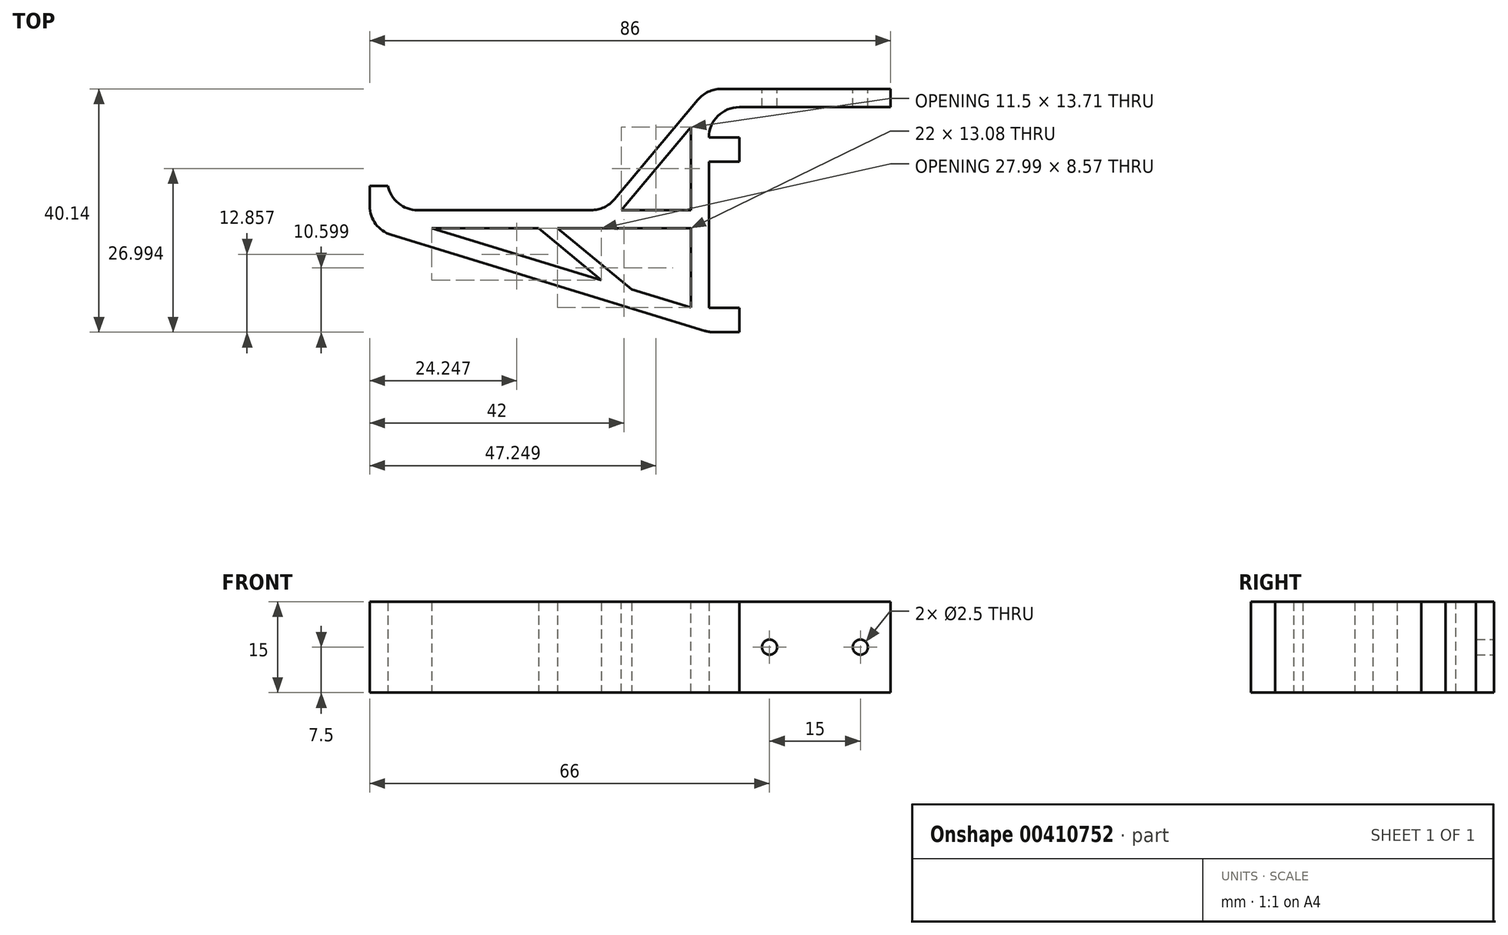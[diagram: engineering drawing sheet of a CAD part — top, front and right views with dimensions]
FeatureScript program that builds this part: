
annotation { "Feature Type Name" : "Feature", "Feature Type Description" : "" }
export const myFeature = defineFeature(function(context is Context, id is Id, definition is map)
    precondition{}
    {
        {
            var Q0;
            Q0=qCreatedBy(makeId("Top.planeOp"),FACE);
            var sketch = newSketch(context, id + "F0", { "sketchPlane" : qUnion([Q0])});
            skLineSegment(sketch, "E0", {"start": v(0, 23) * mm, "end": v(-33, 23) * mm});
            skLineSegment(sketch, "E1", {"start": v(-33, 23) * mm, "end": v(-33, 3) * mm});
            skLineSegment(sketch, "E2", {"start": v(-33, 3) * mm, "end": v(-83, 3) * mm});
            skLineSegment(sketch, "E3", {"start": v(-83, 3) * mm, "end": v(-83, 7) * mm});
            skLineSegment(sketch, "E4", {"start": v(-83, 7) * mm, "end": v(-86, 7) * mm});
            skLineSegment(sketch, "E5", {"start": v(-86, 7) * mm, "end": v(-86, 0) * mm});
            skLineSegment(sketch, "E6", {"start": v(-75.75, 0) * mm, "end": v(-58.14, 0) * mm});
            skLineSegment(sketch, "E7", {"start": v(-30, 0) * mm, "end": v(-30, 20) * mm});
            skLineSegment(sketch, "E8", {"start": v(-30, 20) * mm, "end": v(0, 20) * mm});
            skLineSegment(sketch, "E9", {"start": v(0, 20) * mm, "end": v(0, 23) * mm});
            skLineSegment(sketch, "E10", {"start": v(-86, 0) * mm, "end": v(-30, -17.14) * mm});
            skLineSegment(sketch, "E11", {"start": v(-30, -17.14) * mm, "end": v(-30, -14) * mm});
            skLineSegment(sketch, "E12", {"start": v(-33, -13.08) * mm, "end": v(-42.76, -10.1) * mm});
            skLineSegment(sketch, "E13", {"start": v(-47.76, -8.57) * mm, "end": v(-58.14, 0) * mm});
            skLineSegment(sketch, "E14", {"start": v(-42.76, -10.1) * mm, "end": v(-55, 0) * mm});
            skLineSegment(sketch, "E15.trimOffspring", {"start": v(-55, 0) * mm, "end": v(-33, 0) * mm});
            skLineSegment(sketch, "E16.trimOffspring", {"start": v(-47.76, -8.57) * mm, "end": v(-75.75, 0) * mm});
            skLineSegment(sketch, "E17", {"start": v(-30, -14) * mm, "end": v(-30, 0) * mm});
            skLineSegment(sketch, "E18", {"start": v(-33, -13.08) * mm, "end": v(-33, 0) * mm});
            skSolve(sketch);
        }
        {
            var Q0;
            Q0=makeQuery(id+"F0.imprint","IMPRINT",FACE,{"disambiguationData":[TD([[makeQuery(id+"F0.imprint","IMPRINT",EDGE,{"derivedFrom":sQuery(id+"F0.wireOp",EDGE,"E0")}),1.0]])]});
            extrude(context, id + "F1", {"entities" : qUnion([Q0]), "depth" : 15 * mm});
        }
        {
            var Q0;
            Q0=makeQuery(id+"F1.opExtrude","SWEPT_FACE",FACE,{"disambiguationData":[OSD([sQuery(id+"F0.wireOp",EDGE,"E0")])]});
            var sketch = newSketch(context, id + "F2", { "sketchPlane" : qUnion([Q0])});
            skCircle(sketch, "E19", {"center": v(5, 7.5) * mm, "radius": 1.25 * mm});
            skCircle(sketch, "E20", {"center": v(20, 7.5) * mm, "radius": 1.25 * mm});
            skSolve(sketch);
        }
        {
            var Q0;
            Q0=makeQuery(id+"F2.imprint","IMPRINT",FACE,{"disambiguationData":[TD([[makeQuery(id+"F2.imprint","IMPRINT",EDGE,{"derivedFrom":sQuery(id+"F2.wireOp",EDGE,"E19")}),1.0]])]});
            var Q1;
            Q1=makeQuery(id+"F2.imprint","IMPRINT",FACE,{"disambiguationData":[TD([[makeQuery(id+"F2.imprint","IMPRINT",EDGE,{"derivedFrom":sQuery(id+"F2.wireOp",EDGE,"E20")}),1.0]])]});
            extrude(context, id + "F3", {"entities" : qUnion([Q0, Q1]), "operationType" : NewBodyOperationType.REMOVE, "endBound" : BoundingType.THROUGH_ALL, "oppositeDirection" : true, "depth" : 25 * mm});
        }
        {
            var Q0;
            Q0=makeQuery(id+"F1.opExtrude","SWEPT_EDGE",EDGE,{"disambiguationData":[OSD([sQuery(id+"F0.wireOp",EDGE,"E0"),sQuery(id+"F0.wireOp",EDGE,"E1")])]});
            var Q1;
            Q1=makeQuery(id+"F1.opExtrude","SWEPT_EDGE",EDGE,{"disambiguationData":[OSD([sQuery(id+"F0.wireOp",EDGE,"E7"),sQuery(id+"F0.wireOp",EDGE,"E8")])]});
            fillet(context, id + "F4", {"entities" : qUnion([Q0, Q1]), "tangentPropagation" : true, "radius" : 5 * mm, "defaultsChanged" : false, "vertexSettings" : [], "allowEdgeOverflow" : false});
        }
        {
            var Q0;
            Q0=makeQuery(id+"F1.opExtrude","SWEPT_FACE",FACE,{"disambiguationData":[OSD([sQuery(id+"F0.wireOp",EDGE,"E7"),sQuery(id+"F0.wireOp",EDGE,"E11"),sQuery(id+"F0.wireOp",EDGE,"E17")])]});
            var sketch = newSketch(context, id + "F5", { "sketchPlane" : qUnion([Q0])});
            skLineSegment(sketch, "E21.bottom", {"start": v(-17.14, 15) * mm, "end": v(-13.14, 15) * mm});
            skLineSegment(sketch, "E21.top", {"start": v(-17.14, 0) * mm, "end": v(-13.14, 0) * mm});
            skLineSegment(sketch, "E21.left", {"start": v(-17.14, 15) * mm, "end": v(-17.14, 0) * mm});
            skLineSegment(sketch, "E21.right", {"start": v(-13.14, 15) * mm, "end": v(-13.14, 0) * mm});
            skLineSegment(sketch, "E22.bottom", {"start": v(15, 15) * mm, "end": v(11, 15) * mm});
            skLineSegment(sketch, "E22.top", {"start": v(15, 0) * mm, "end": v(11, 0) * mm});
            skLineSegment(sketch, "E22.left", {"start": v(15, 15) * mm, "end": v(15, 0) * mm});
            skLineSegment(sketch, "E22.right", {"start": v(11, 15) * mm, "end": v(11, 0) * mm});
            skSolve(sketch);
        }
        {
            var Q0;
            Q0=makeQuery(id+"F5.imprint","IMPRINT",FACE,{"disambiguationData":[TD([[makeQuery(id+"F5.imprint","IMPRINT",EDGE,{"derivedFrom":sQuery(id+"F5.wireOp",EDGE,"E21.bottom")}),-1.0]])]});
            var Q1;
            Q1=makeQuery(id+"F5.imprint","IMPRINT",FACE,{"disambiguationData":[TD([[makeQuery(id+"F5.imprint","IMPRINT",EDGE,{"derivedFrom":sQuery(id+"F5.wireOp",EDGE,"E22.bottom")}),-1.0]])]});
            extrude(context, id + "F6", {"entities" : qUnion([Q0, Q1]), "operationType" : NewBodyOperationType.ADD, "depth" : 5 * mm, "offsetDistance" : 25 * mm});
        }
        {
            var Q0;
            Q0=makeQuery(id+"F6.boolean.opBoolean","MERGE",FACE,{"derivedFrom":[makeQuery(id+"F1.opExtrude","CAP_FACE",FACE,{"disambiguationData":[OSD([sQuery(id+"F0.wireOp",EDGE,"E0"),sQuery(id+"F0.wireOp",EDGE,"E1"),sQuery(id+"F0.wireOp",EDGE,"E2"),sQuery(id+"F0.wireOp",EDGE,"E3"),sQuery(id+"F0.wireOp",EDGE,"E4"),sQuery(id+"F0.wireOp",EDGE,"E5"),sQuery(id+"F0.wireOp",EDGE,"E6"),sQuery(id+"F0.wireOp",EDGE,"E7"),sQuery(id+"F0.wireOp",EDGE,"E8"),sQuery(id+"F0.wireOp",EDGE,"E9"),sQuery(id+"F0.wireOp",EDGE,"E10"),sQuery(id+"F0.wireOp",EDGE,"E11"),sQuery(id+"F0.wireOp",EDGE,"E12"),sQuery(id+"F0.wireOp",EDGE,"E13"),sQuery(id+"F0.wireOp",EDGE,"E14"),sQuery(id+"F0.wireOp",EDGE,"E15.trimOffspring"),sQuery(id+"F0.wireOp",EDGE,"E16.trimOffspring"),sQuery(id+"F0.wireOp",EDGE,"E17"),sQuery(id+"F0.wireOp",EDGE,"E18")])],"isStart":false}),makeQuery(id+"F6.opExtrude","SWEPT_FACE",FACE,{"disambiguationData":[OSD([sQuery(id+"F5.wireOp",EDGE,"E21.bottom")])]}),makeQuery(id+"F6.opExtrude","SWEPT_FACE",FACE,{"disambiguationData":[OSD([sQuery(id+"F5.wireOp",EDGE,"E22.bottom")])]})]});
            var sketch = newSketch(context, id + "F7", { "sketchPlane" : qUnion([Q0])});
            skLineSegment(sketch, "E23", {"start": v(-47.11, 3) * mm, "end": v(-31.83, 21.21) * mm});
            skLineSegment(sketch, "E24", {"start": v(-31.83, 21.21) * mm, "end": v(-31.83, 18.1) * mm});
            skLineSegment(sketch, "E25", {"start": v(-31.83, 18.1) * mm, "end": v(-44.5, 3) * mm});
            skLineSegment(sketch, "E26", {"start": v(-44.5, 3) * mm, "end": v(-47.11, 3) * mm});
            skSolve(sketch);
        }
        {
            var Q0;
            {var subQ9=sQuery(id+"F7.wireOp",EDGE,"E23");Q0=makeQuery(id+"F7.imprint","IMPRINT",FACE,{"disambiguationData":[TD([[makeQuery(id+"F7.imprint","IMPRINT",EDGE,{"derivedFrom":subQ9}),-1.0]])]});}
            var Q1;
            Q1=makeQuery(id+"F6.boolean.opBoolean","MERGE",FACE,{"derivedFrom":[makeQuery(id+"F1.opExtrude","CAP_FACE",FACE,{"disambiguationData":[OSD([sQuery(id+"F0.wireOp",EDGE,"E0"),sQuery(id+"F0.wireOp",EDGE,"E1"),sQuery(id+"F0.wireOp",EDGE,"E2"),sQuery(id+"F0.wireOp",EDGE,"E3"),sQuery(id+"F0.wireOp",EDGE,"E4"),sQuery(id+"F0.wireOp",EDGE,"E5"),sQuery(id+"F0.wireOp",EDGE,"E6"),sQuery(id+"F0.wireOp",EDGE,"E7"),sQuery(id+"F0.wireOp",EDGE,"E8"),sQuery(id+"F0.wireOp",EDGE,"E9"),sQuery(id+"F0.wireOp",EDGE,"E10"),sQuery(id+"F0.wireOp",EDGE,"E11"),sQuery(id+"F0.wireOp",EDGE,"E12"),sQuery(id+"F0.wireOp",EDGE,"E13"),sQuery(id+"F0.wireOp",EDGE,"E14"),sQuery(id+"F0.wireOp",EDGE,"E15.trimOffspring"),sQuery(id+"F0.wireOp",EDGE,"E16.trimOffspring"),sQuery(id+"F0.wireOp",EDGE,"E17"),sQuery(id+"F0.wireOp",EDGE,"E18")])],"isStart":true}),makeQuery(id+"F6.opExtrude","SWEPT_FACE",FACE,{"disambiguationData":[OSD([sQuery(id+"F5.wireOp",EDGE,"E21.top")])]}),makeQuery(id+"F6.opExtrude","SWEPT_FACE",FACE,{"disambiguationData":[OSD([sQuery(id+"F5.wireOp",EDGE,"E22.top")])]})]});
            extrude(context, id + "F8", {"entities" : qUnion([Q0]), "operationType" : NewBodyOperationType.ADD, "endBound" : BoundingType.UP_TO_SURFACE, "oppositeDirection" : true, "depth" : 25 * mm, "endBoundEntityFace" : qUnion([Q1]), "offsetDistance" : 25 * mm});
        }
        {
            var Q0;
            Q0=makeQuery(id+"F1.opExtrude","SWEPT_EDGE",EDGE,{"disambiguationData":[OSD([sQuery(id+"F0.wireOp",EDGE,"E5"),sQuery(id+"F0.wireOp",EDGE,"E10")])]});
            var Q1;
            Q1=makeQuery(id+"F6.boolean.opBoolean","MERGE",EDGE,{"derivedFrom":[makeQuery(id+"F1.opExtrude","SWEPT_EDGE",EDGE,{"disambiguationData":[OSD([sQuery(id+"F0.wireOp",EDGE,"E10"),sQuery(id+"F0.wireOp",EDGE,"E11")])]}),makeQuery(id+"F6.opExtrude","CAP_EDGE",EDGE,{"disambiguationData":[OSD([sQuery(id+"F5.wireOp",EDGE,"E21.left")])],"isStart":true})]});
            var Q2;
            Q2=makeQuery(id+"F1.opExtrude","SWEPT_EDGE",EDGE,{"disambiguationData":[OSD([sQuery(id+"F0.wireOp",EDGE,"E2"),sQuery(id+"F0.wireOp",EDGE,"E3")])]});
            var Q3;
            Q3=makeQuery(id+"F8.opExtrude","SWEPT_EDGE",EDGE,{"disambiguationData":[OSD([sQuery(id+"F0.wireOp",EDGE,"E2"),sQuery(id+"F7.wireOp",EDGE,"E23"),sQuery(id+"F7.wireOp",EDGE,"E26")])]});
            fillet(context, id + "F9", {"entities" : qUnion([Q0, Q1, Q2, Q3]), "tangentPropagation" : true, "radius" : 5 * mm, "defaultsChanged" : false, "vertexSettings" : [], "allowEdgeOverflow" : false});
        }
    });
